# Revit family: Door-MultiGlide-Andersen-Traditional_Clad-Exterior_Stacking
name_source: partatom
category: Doors
revit_build: Autodesk Revit 2014 (Build: 20140709_2115(x64)
units: mm (PartAtom-declared; Revit-internal decimal feet)

## types (1)
- Door-MultiGlide-Andersen-Traditional_Clad-Exterior_Stacking
    - Bottom Bar Location (Modified Colonial/Fractional) = 2' - 0"
    - Lights High = 5
    - Lights Wide = 4
    Exterior Finish = Aluminum - Andersen - Painted - Colony White
    Finished Floor Thickness (Required for Flush Sill) = 0' - 0 1/4"
    Frame Setback Frome Exterior Wall Surface = 0' - 2"
    Function = Interior
    Grille Bar Size                                                                                                                                                                                                         . = Grilles : 7/8" Full Divided Light
    Grille Pattern                                                                                                                                                                                                         . = Grille Pattern : No Grilles
    Height = 7' - 11 1/2"
    Interior Finish = Wood - Andersen - Pine
    Jamb Depth = 1' - 5 7/8"
    Panel Configuration                                                                                                    . = One-Directional : 06 Panel
    Panel Type                                                                                                    . = Panel : Traditional Clad (8" Bottom Rail)
    Rough Header Height (From Top of Sub-Floor) = 8' - 0"
    Rough Height = 8' - 0"
    Rough Width = 25' - 0"
    Screen Option                                                                                                    . = Screen : Single Panel
    Show Panels in Open Position = No
    Show Screens in Open Position = No
    Sill Type                                                                                                    . = On-Floor Drainage : No Accessories
    Size Limitation (Panel) = Size Okay
    Size Limitation (Unit) = Size Okay
    Wall Closure = By host
    Width = 24' - 11"
    XA1D02P = One-Directional : 02 Panel
    XA1D03P = One-Directional : 03 Panel
    XA1D04P = One-Directional : 04 Panel
    XA1D05P = One-Directional : 05 Panel
    XA1D06P = One-Directional : 06 Panel
    XABottomRail02 = Panel : Contemporary Clad
    XABottomRail04 = Panel : Traditional Clad (4 11/16" Bottom Rail)
    XABottomRail08 = Panel : Traditional Clad (8" Bottom Rail)
    XABottomRail12 = Panel : Traditional Clad (12" Bottom Rail)
    XAFlushNoAccessories = Flush : No Accessories Available
    XAOnFloorExtIntRamp = On-Floor Drainage : with Exterior and Interior Ramp
    XAOnFloorExtRamp = On-Floor Drainage : with Exterior Ramp
    XAOnFloorExtRampRaised = On-Floor Drainage : with Exterior Ramp and Raised Threshold
    XAOnFloorIntRamp = On-Floor Drainage : with Interior Ramp
    XAOnFloorNoAccessories = On-Floor Drainage : No Accessories
    XAOnFloorRaised = On-Floor Drainage : with Raised Threshold
    XAScreenMultiple = Screen : Single Panel
    XAScreenNone = Screen : None
    XBGrillePattern = Grille Pattern : No Grilles
    XBGrilleSize = Grilles : 7/8" Full Divided Light
    XBPanelConfiguration = One-Directional : 06 Panel
    XBPanelType = Panel : Traditional Clad (8" Bottom Rail)
    XBScreen = Screen : Single Panel
    XBSill = On-Floor Drainage : No Accessories
    XCGrillePattern_ = 0
    XCGrilleSize = 4
    XCGrilleSize_ = 0' - 0 7/8"
    XCHeadLength_ = 24' - 7 1/4"
    XCJambLength_ = 7' - 10 3/4"
    XCSillLength_ = 24' - 11"
    XCladSetbackLeft = 1' - 3"
    XCladSetbackRight = 0' - 2 1/2"
    XDapOut = 0' - 0"
    XDapOutBack = 0' - 0"
    XDapOutFront = 0' - 0 3/4"
    XDapOutHeight = 0' - 0 3/4"
    XDapOutOffset = 0' - 1"
    XFlushTrackPositionPanel = 1' - 0 1/2"
    XFlushTrackPositionScreen = 0' - 2"
    XFlushTrackPositionScreen2 = 0' - 0"
    XFlushTrackVisibility = No
    XFlushTrackVisibility1 = No
    XFlushTrackVisibility2 = No
    XFlushTrackVisibility3 = No
    XFlushTrackVisibility4 = No
    XFlushTrackVisibility5 = No
    XFlushTrackVisibilityA1 = No
    XFlushTrackVisibilityA2 = No
    XFlushTrackVisibilityA3 = No
    XFlushTrackVisibilityA4 = No
    XFlushTrackVisibilityA5 = No
    XFlushTrackVisibilityScreen = No
    XFlushTrackVisibilityScreen2 = No
    XFlushTrackVisibilityScreen3 = No
    XFlushTrackVisibilityScreen4 = No
    XFlushTrackVisibilityScreen5 = No
    XFlushTrackVisibilityScreenA2 = No
    XFlushTrackVisibilityScreenA3 = No
    XFlushTrackVisibilityScreenA4 = No
    XFlushTrackVisibilityScreenA5 = No
    XGColonial = Grille Pattern : Colonial
    XGFDL1 1_2 = Grilles : 1 1/2" Full Divided Light
    XGFDL1 1_8 = Grilles : 1 1/8" Full Divided Light
    XGFDL7_8 = Grilles : 7/8" Full Divided Light
    XGGBG1 = Grilles : 1" Contoured Grilles Between Glass
    XGGBG5_8 = Grilles : 5/8" Flat Grilles Between Glass
    XGModifiedColonial = Grille Pattern : Modified Colonial/Fractional
    XGNoGrilles = Grille Pattern : No Grilles
    XGPrairie = Grille Pattern : Prairie
    XGSDL1 1_2 = Grilles : 1 1/2" Simulated Divided Light
    XGSDL1 1_8 = Grilles : 1 1/8" Simulated Divided Light
    XGSDL7_8 = Grilles : 7/8" Simulated Divided Light
    XInteriorStackingLockJamb = 0' - 2 5/8"
    XJambCladQuantityLeft = 6
    XJambCladQuantityRight = 2
    XJambLineLeftExtStops = No
    XJambLineLeftLockPanel = Yes
    XJambLineLeftLockScreen = No
    XJambLineLeftMidStops = No
    XJambLineLeftScreenLock = Yes
    XJambLineRightExtPanel = No
    XJambLineRightExtStops = No
    XJambLineRightIntPanel = No
    XJambLineRightMidStops = Yes
    XJambLockPanel = No
    XJambLockScreen = No
    XJambStatPanel1 = No
    XJambStatPanel2 = Yes
    XJambStatPanel3 = No
    XJambStatPanel4 = No
    XJambWoodQuantityLeft = 2
    XJambWoodQuantityRight = 6
    XOnFloorVisibility = Yes
    XPanel1Location = 4' - 7 5/32"
    XPanel2Location = 8' - 7 1/2"
    XPanel3Location = 12' - 7 27/32"
    XPanel4Location = 16' - 8 3/16"
    XPanel5Location = 20' - 8 17/32"
    XPanelHeight = 7' - 8 1/2"
    XPanelLeadPositionX = 24' - 8 7/8"
    XPanelLeadPositionZ = 1' - 3"
    XPanelSizeBottomRail = 0' - 8"
    XPanelSizeStile = 0' - 4 11/16"
    XPanelSizeTopRail = 0' - 4 11/16"
    XPanelVisibilityTwoDirectional = No
    XPanelWidth = 4' - 5 1/32"
    XScreen1Location = 8' - 6 7/32"
    XScreen2Location = 8' - 6 7/32"
    XScreen3Location = 12' - 6 7/8"
    XScreen4Location = 16' - 7 17/32"
    XScreen5Location = 20' - 8 7/32"
    XScreenLeadPositionX = 24' - 8 7/8"
    XScreenLeadPositionZ = 0' - 0"
    XScreenNo = No
    XScreenQuantity = 2
    XScreenVisibility = Yes
    XScreenVisibilityOneDirectional = Yes
    XScreenVisibilityTwoDirectional = No
    XScreenWidth = 4' - 3 13/32"
    XSillAccessoryExtRampDim = 0' - 0 3/4"
    XSillAccessoryExtRampVisibility = No
    XSillAccessoryIntRampDim = 0' - 0"
    XSillAccessoryIntRampVisibility = No
    XSillAccessoryRaisedThresholdVisibility = No
    XSizeLimitationPanel = 0
    XSizeLimitationUnit = 0
    XSizeVerification = Yes
    XTrackQuantityPanel = 6
    XTrackQuantityScreen = 1
    XTrackQuantityTotal = 7
    XTwoDirectional = No

## geometry (parser evidence)
native form markers: Sweep x14
no freeform markers — native parametric forms only
